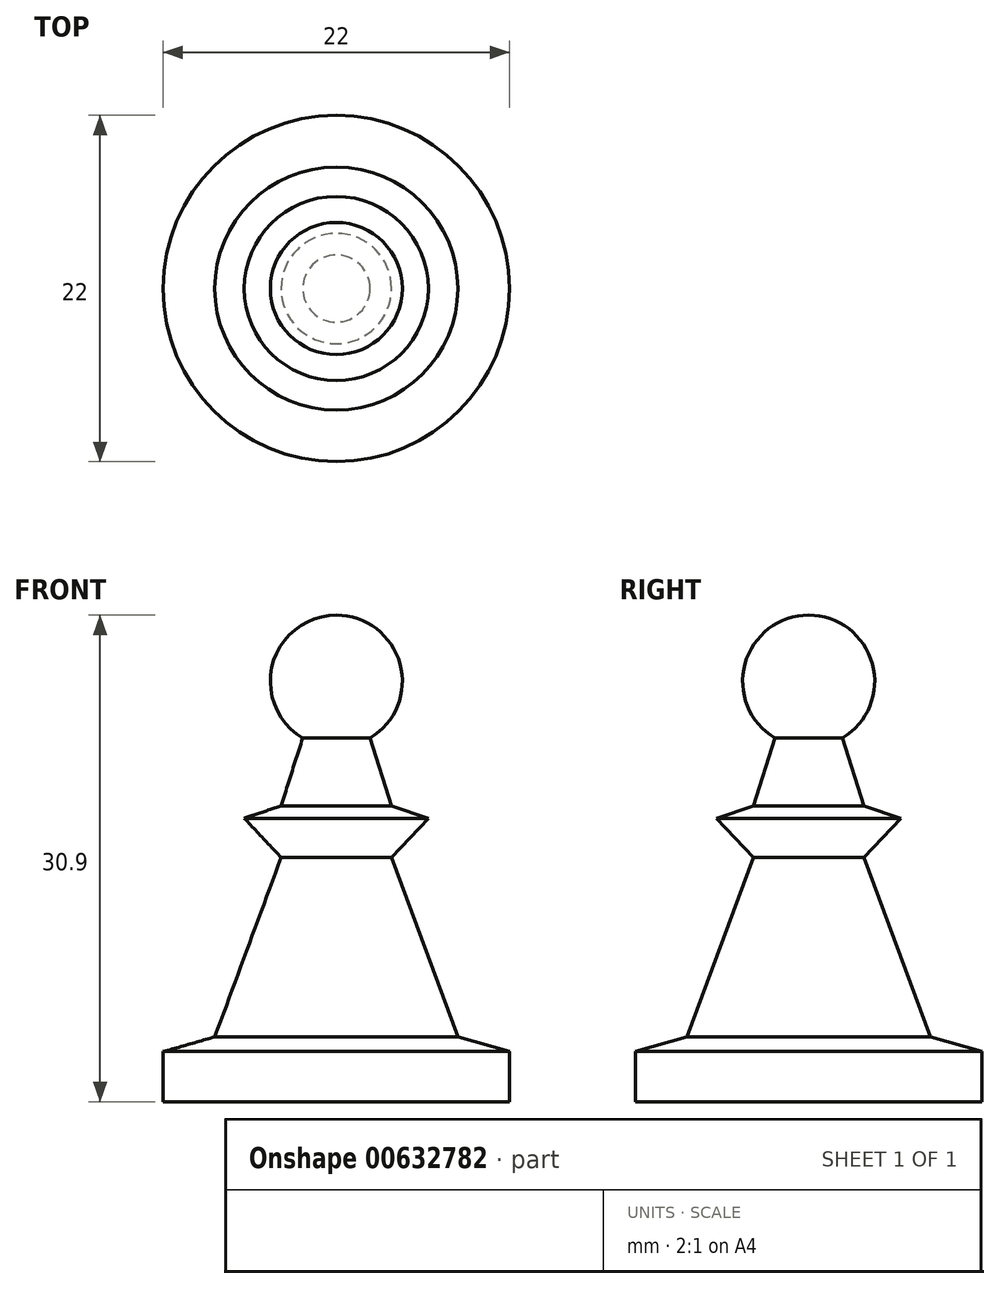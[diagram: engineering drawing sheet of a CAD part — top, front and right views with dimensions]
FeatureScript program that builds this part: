
annotation { "Feature Type Name" : "Feature", "Feature Type Description" : "" }
export const myFeature = defineFeature(function(context is Context, id is Id, definition is map)
    precondition{}
    {
        {
            var Q0;
            Q0=qCreatedBy(makeId("Front.planeOp"),FACE);
            var sketch = newSketch(context, id + "F0", { "sketchPlane" : qUnion([Q0])});
            skArc(sketch, "E0", {"start": v(0, 30.9) * mm, "mid": v(-4.04, 27.81) * mm, "end": v(-2.14, 23.1) * mm});
            skLineSegment(sketch, "E1", {"start": v(0, 0) * mm, "end": v(0, 30.9) * mm});
            skPoint(sketch, "E2", {"position": v(0, 22.51) * mm});
            skLineSegment(sketch, "E3", {"start": v(-2.14, 23.1) * mm, "end": v(-3.5, 18.79) * mm});
            skLineSegment(sketch, "E4", {"start": v(-3.5, 18.79) * mm, "end": v(-5.85, 18) * mm});
            skLineSegment(sketch, "E5", {"start": v(-5.85, 18) * mm, "end": v(-3.5, 15.5) * mm});
            skLineSegment(sketch, "E6", {"start": v(-3.5, 15.5) * mm, "end": v(-7.72, 4.12) * mm});
            skLineSegment(sketch, "E7", {"start": v(-7.72, 4.12) * mm, "end": v(-11, 3.18) * mm});
            skLineSegment(sketch, "E8", {"start": v(-11, 3.18) * mm, "end": v(-11, 0) * mm});
            skLineSegment(sketch, "E9", {"start": v(0, 0) * mm, "end": v(-11, 0) * mm});
            skSolve(sketch);
        }
        {
            var Q0;
            Q0=makeQuery(id+"F0.imprint","IMPRINT",FACE,{"disambiguationData":[TD([[makeQuery(id+"F0.imprint","IMPRINT",EDGE,{"derivedFrom":sQuery(id+"F0.wireOp",EDGE,"E0")}),1.0]])]});
            var Q1;
            Q1=sQuery(id+"F0.wireOp",EDGE,"E1");
            revolve(context, id + "F1", {"entities" : qUnion([Q0]), "axis" : qUnion([Q1]), "revolveType" : RevolveType.FULL});
        }
    });
